# Revit family: FIXEE50
name_source: partatom
category: Structural Connections
revit_build: Autodesk Revit 2015 (Build: 20140606_1530(x64)
units: mm (PartAtom-declared; Revit-internal decimal feet)

## types (1)
- FIXEE50
    Default Elevation = 0 mm  [stored 0 ft]
    Density = 0.45 kg
    Description = washer
    EPD = https://www.strongtie.eu
    ETA / DoP = https://www.strongtie.eu
    Manufacturer = Simpson Strong-Tie
    Model = FIX EE50
    Model Disclaimer = Contact Simpson Strong-Tie Company  for more information
    Model ID = 0315264581781406971568527697323240232095
    Name = FIX EE50
    ObjectType = FIX EE50
    Product Material = HotDipGalvanised
    Product Type = washer
    Reference = FIX EE50
    Technical datasheet = https://www.strongtie.eu
    URL = www.strongtie.eu
    UniClass Number = Pr_20_29_31_13
    UniClass Title = Carbon steel punched metal plate fasteners

note: [stored X ft] marks values corroborated as IEEE doubles in the binary element streams (Revit-internal decimal feet)

## geometry (parser evidence)
native form markers: Blend x24, Sweep x3
no freeform markers — native parametric forms only
